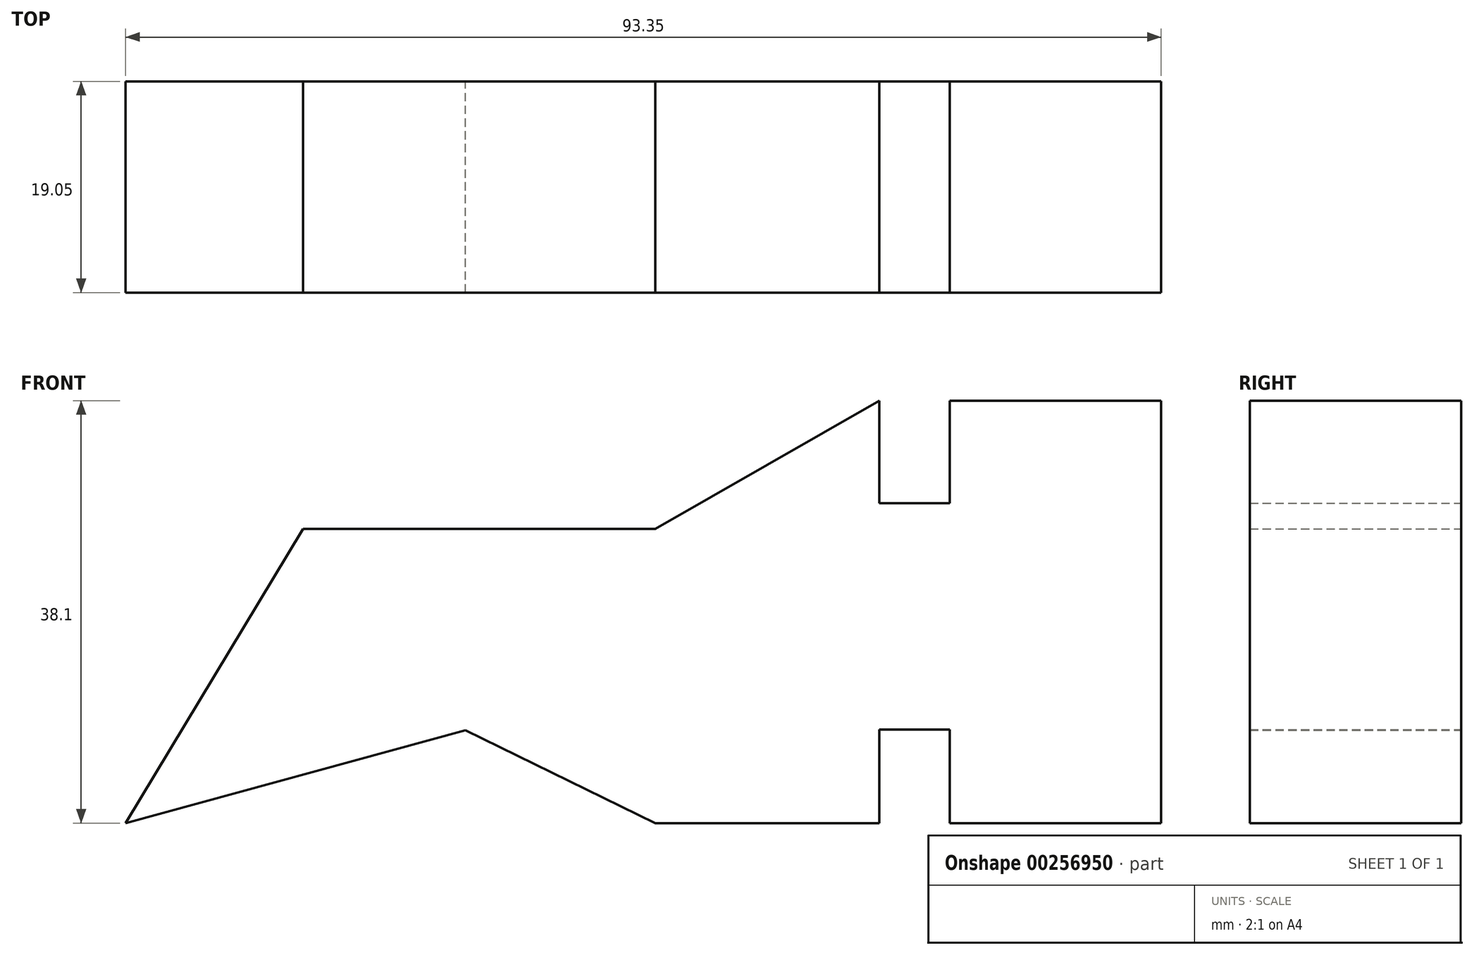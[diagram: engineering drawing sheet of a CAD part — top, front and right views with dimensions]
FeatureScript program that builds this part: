
annotation { "Feature Type Name" : "Feature", "Feature Type Description" : "" }
export const myFeature = defineFeature(function(context is Context, id is Id, definition is map)
    precondition{}
    {
        {
            var Q0;
            Q0=qCreatedBy(makeId("Front.planeOp"),FACE);
            var sketch = newSketch(context, id + "F0", { "sketchPlane" : qUnion([Q0])});
            skLineSegment(sketch, "E0", {"start": v(0, 0) * mm, "end": v(20.2, 0) * mm});
            skLineSegment(sketch, "E1", {"start": v(20.2, 0) * mm, "end": v(20.2, 8.42) * mm});
            skLineSegment(sketch, "E2", {"start": v(20.2, 8.42) * mm, "end": v(26.56, 8.42) * mm});
            skLineSegment(sketch, "E3", {"start": v(26.56, 8.42) * mm, "end": v(26.56, 0) * mm});
            skLineSegment(sketch, "E4", {"start": v(26.56, 0) * mm, "end": v(45.6, 0) * mm});
            skLineSegment(sketch, "E5", {"start": v(45.6, 0) * mm, "end": v(45.6, 38.1) * mm});
            skLineSegment(sketch, "E6", {"start": v(45.6, 38.1) * mm, "end": v(26.56, 38.1) * mm});
            skLineSegment(sketch, "E7", {"start": v(26.56, 38.1) * mm, "end": v(26.56, 28.84) * mm});
            skLineSegment(sketch, "E8", {"start": v(26.56, 28.84) * mm, "end": v(20.2, 28.84) * mm});
            skLineSegment(sketch, "E9", {"start": v(20.2, 28.84) * mm, "end": v(20.2, 38.1) * mm});
            skLineSegment(sketch, "E10", {"start": v(20.2, 38.1) * mm, "end": v(0, 26.52) * mm});
            skLineSegment(sketch, "E11", {"start": v(0, 26.52) * mm, "end": v(-31.75, 26.52) * mm});
            skLineSegment(sketch, "E12", {"start": v(-31.75, 26.52) * mm, "end": v(-47.74, 0) * mm});
            skLineSegment(sketch, "E13", {"start": v(-47.74, 0) * mm, "end": v(-17.11, 8.37) * mm});
            skLineSegment(sketch, "E14", {"start": v(-17.11, 8.37) * mm, "end": v(0, 0) * mm});
            skSolve(sketch);
        }
        {
            var Q0;
            Q0=makeQuery(id+"F0.imprint","IMPRINT",FACE,{"disambiguationData":[TD([[makeQuery(id+"F0.imprint","IMPRINT",EDGE,{"derivedFrom":sQuery(id+"F0.wireOp",EDGE,"E0")}),1.0]])]});
            extrude(context, id + "F1", {"entities" : qUnion([Q0]), "depth" : 19.05 * mm});
        }
    });
